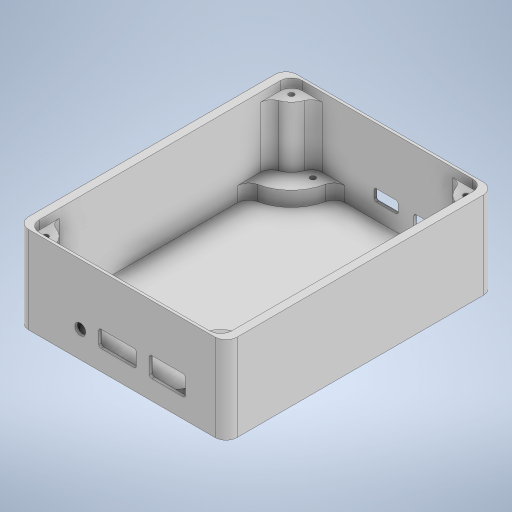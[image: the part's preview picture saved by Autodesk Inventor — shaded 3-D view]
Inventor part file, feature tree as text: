
AUTODESK INVENTOR PART (.ipt)
format: ipt  version: 2024 (Build 280153000, 153)  size: 585,728 bytes
history: native  units: mm
features: other x44, projected_geometry x7, sketch x6, extrude x6, hole x2
ambient origin geometry x8: Origin, YZ Plane, XZ Plane, XY Plane, X Axis, Y Axis, Z Axis, Center Point
bodies: 实体1 (feature_tree)
feature tree (65):
  sketch  "草图1"  dims[d0=122.78mm d1=95.4mm]
  extrude  "拉伸1"  Depth=95.4mm
  extrude  "拉伸2"  Depth=88.0mm
  extrude  "拉伸3"  TaperAngle=90.0deg  [1 undecoded]
  extrude  "拉伸4"  TaperAngle=90.0deg  [1 undecoded]
  hole  "孔3"  [1 undecoded]
  hole  "孔5"  [1 undecoded]
  other  "面圆角1"
  other  "面圆角2"
  other  "面圆角3"
  other  "面圆角4"
  other  "面圆角5"
  other  "面圆角6"
  other  "面圆角7"
  other  "面圆角8"
  other  "面圆角9"
  other  "面圆角10"
  other  "面圆角11"
  other  "面圆角12"
  other  "面圆角13"
  other  "面圆角14"
  other  "面圆角15"
  other  "面圆角16"
  other  "面圆角17"
  other  "面圆角18"
  other  "面圆角19"
  other  "面圆角20"
  other  "面圆角21"
  other  "面圆角22"
  other  "面圆角23"
  other  "面圆角24"
  extrude  "拉伸5"  Depth=1.0mm
  other  "面圆角25"
  other  "面圆角26"
  other  "面圆角27"
  other  "面圆角28"
  other  "面圆角29"
  other  "面圆角30"
  other  "面圆角31"
  other  "面圆角32"
  sketch  "草图8"  dims[d8=55.88mm d9=29.848mm]
  extrude  "拉伸6"  Depth=1.0mm
  other  "面圆角33"
  other  "面圆角34"
  other  "面圆角35"
  other  "面圆角36"
  other  "面圆角37"
  other  "面圆角38"
  other  "面圆角39"
  other  "面圆角40"
  sketch  "草图3"  dims[d2=120.38mm d3=88.0mm]
  sketch  "草图6"  dims[d4=20.0mm d5=90.0deg]
  projected_geometry  "投影回路6"
  sketch  "草图7"  dims[d6=10.0mm d7=90.0deg]
  projected_geometry  "投影回路7"
  projected_geometry  "投影回路8"
  projected_geometry  "投影回路9"
  sketch  "草图9"  dims[d10=4.0mm d11=4.0mm d12=2.5mm d13=2.5mm d14=39.8mm d15=0.0mm d16=1.2mm d17=0.0mm d18=8.0mm d19=0.0mm d20=35.8mm d21=0.0mm d36=2.459mm d37=6.0mm d38=4.0mm d39=2.0mm d40=90.0deg d41=6.0mm d42=20.594885mm d50=4.0mm d51=4.0mm d52=2.459mm d53=6.0mm d54=4.0mm d55=2.0mm d56=90.0deg d57=6.0mm d58=20.594885mm d59=5.0mm d60=5.0mm d61=5.0mm d62=5.0mm d63=5.0mm d64=5.0mm d65=5.0mm d66=5.0mm d67=5.0mm d68=5.0mm d69=5.0mm d70=5.0mm d71=5.0mm d72=5.0mm d73=5.0mm d74=5.0mm d75=5.0mm d76=5.0mm d77=5.0mm d78=5.0mm d79=5.0mm d80=5.0mm d81=5.0mm d82=5.0mm d84=1.6mm d85=18.415mm d86=0.95mm d87=10.05mm d88=16.4mm d89=4.445mm d90=1.3mm d91=8.85mm d92=17.1mm d93=21.463mm d94=4.1mm d95=5.0mm d96=20.0mm d97=0.0mm d98=1.0mm d99=1.0mm d100=1.0mm d101=1.0mm d102=1.0mm d103=1.0mm d104=1.0mm d105=1.0mm d106=1.6mm d107=0.8mm d108=19.177mm d109=3.94mm d110=5.26mm d111=7.125mm d112=7.125mm d113=0.635mm d114=1.65mm d115=11.0mm d116=5.3mm d117=20.0mm d118=0.0mm d119=1.0mm d120=1.0mm d121=1.0mm d122=1.0mm d123=1.0mm d124=1.0mm d125=1.0mm d126=1.0mm d22=1.0mm d23=1.0mm d24=6.5mm d25=0.15mm d26=3.0mm d27=0.375mm d28=14.3117mm d29=6.0mm d30=20.594885mm d31=0.0625mm d32=0.75mm d33=0.375mm d43=0.75mm d44=20.594885mm d45=0.0625mm d46=0.75mm d47=0.375mm]
  projected_geometry  "投影回路10"
  projected_geometry  "投影回路11"
  projected_geometry  "投影回路12"
  other  "投影剖切边1"
  other  "投影剖切边2"
  other  "投影剖切边16"
  other  "投影剖切边17"
note: 4 required parameter values undecoded (feature->parameter linkage not recoverable at this tier; creation-order binding heuristic only, values carry confidence <= 0.55)
